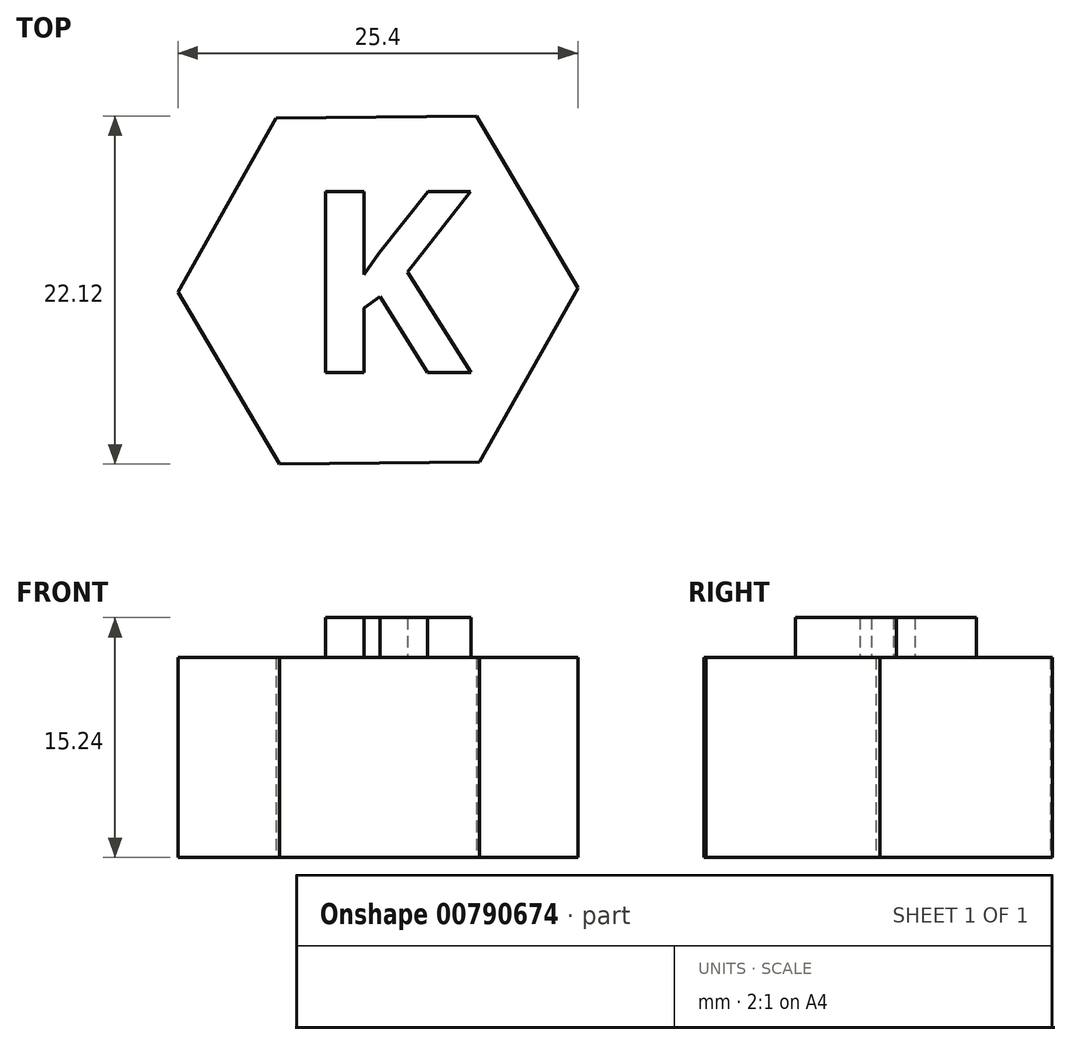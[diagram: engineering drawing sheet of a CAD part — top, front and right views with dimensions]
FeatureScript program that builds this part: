
annotation { "Feature Type Name" : "Feature", "Feature Type Description" : "" }
export const myFeature = defineFeature(function(context is Context, id is Id, definition is map)
    precondition{}
    {
        {
            var Q0;
            Q0=qCreatedBy(makeId("Top.planeOp"),FACE);
            var sketch = newSketch(context, id + "F0", { "sketchPlane" : qUnion([Q0])});
            skCircle(sketch, "E0.cCircle", {"center": v(0, 0) * mm, "radius": 11 * mm, "construction": true});
            skLineSegment(sketch, "E0.0", {"start": v(6.24, 11.06) * mm, "end": v(12.7, 0.13) * mm});
            skLineSegment(sketch, "E0.1", {"start": v(12.7, 0.13) * mm, "end": v(6.46, -10.94) * mm});
            skLineSegment(sketch, "E0.2", {"start": v(6.46, -10.94) * mm, "end": v(-6.24, -11.06) * mm});
            skLineSegment(sketch, "E0.3", {"start": v(-6.24, -11.06) * mm, "end": v(-12.7, -0.13) * mm});
            skLineSegment(sketch, "E0.4", {"start": v(-12.7, -0.13) * mm, "end": v(-6.46, 10.94) * mm});
            skLineSegment(sketch, "E0.5", {"start": v(-6.46, 10.94) * mm, "end": v(6.24, 11.06) * mm});
            skPoint(sketch, "E0.0.midPoint", {"position": v(9.47, 5.6) * mm});
            skSolve(sketch);
        }
        {
            var Q0;
            Q0 = qSketchRegion(id + "F0", true);
            extrude(context, id + "F1", {"entities" : qUnion([Q0]), "depth" : 12.7 * mm, "offsetDistance" : 25.4 * mm});
        }
        {
            var Q0;
            Q0=makeQuery(id+"F1.opExtrude","CAP_FACE",FACE,{"disambiguationData":[OSD([sQuery(id+"F0.wireOp",EDGE,"E0.0"),sQuery(id+"F0.wireOp",EDGE,"E0.1"),sQuery(id+"F0.wireOp",EDGE,"E0.2"),sQuery(id+"F0.wireOp",EDGE,"E0.3"),sQuery(id+"F0.wireOp",EDGE,"E0.4"),sQuery(id+"F0.wireOp",EDGE,"E0.5")])],"isStart":false});
            var sketch = newSketch(context, id + "F2", { "sketchPlane" : qUnion([Q0])});
            skText(sketch, "E1", { "text": "K", "fontName": "OpenSans-Bold.ttf"});
            const initialGuessF2  = {"E1": [-0.00478, -0.00525, 1, 0, 0.01159]};
            skSetInitialGuess(sketch, initialGuessF2);
            skSolve(sketch);
        }
        {
            var Q0;
            Q0 = qSketchRegion(id + "F2", true);
            extrude(context, id + "F3", {"entities" : qUnion([Q0]), "operationType" : NewBodyOperationType.ADD, "depth" : 2.54 * mm, "offsetDistance" : 25.4 * mm});
        }
    });
